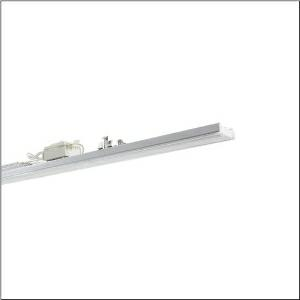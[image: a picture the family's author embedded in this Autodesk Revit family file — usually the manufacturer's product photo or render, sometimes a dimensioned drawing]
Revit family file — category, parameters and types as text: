
# Revit family: licross_21_recessed_mo_52te14dv4exg
name_source: partatom
category: Lighting Fixtures
units: mm (PartAtom-declared; Revit-internal decimal feet)

## family parameters
Cut with Voids When Loaded = No
Host = Face
Light Source = No
Part Type = Normal
Room Calculation Point = No
Round Connector Dimension = Use Diameter
Shared = No

## types (1)
- --- (1 x LED, 14200 lm, 85.3 W, 4000K)
    Apparent Load = 85 VA
    CIE Flux Codes = 56 84 97 100 100
    Color Rendering = 80
    Color Temperature = 4000K
    Default Elevation = 1800 mm
    Description = Licross 21 Recessed MO, luminaire insert, of sheet steel, galvanised, coil coated, white, length: 2.250mm, width: 66mm, height: 67mm, LED rated luminous flux: 14.200lm, light colour: 840, SDCM (Standard Deviation of Colour Matching)MacAdam ≤ 3 SDCM (initial), control gear: DALI 2, with plug, 5-pole, with phase selection, mains connection: 220..240V, AC, 50/60Hz, rated input power: 85W, internal wiring halogen-free, primary light control with lens, of plastic, primary optical cover: cover, of PMMA, light emission: direct distribution, primary light characteristic: asymmetric, protection rating (complete): IP54, insulation class (complete): insulation class I (protective earthing), certification: CE, ENEC, VDE, UKCA, protection symbol: D if used in an environment with non-conductive dust loads with corresponding accessories, impact resistance: IK06, permissible ambient temperature for indoor applications: -25..+35°C, corresponds to IFS (International Featured Standards) requirements for safety and quality in the food industry, reducing of maximum allowable ambient temperature of 5°C with ceiling mounting, LABS conformity tested according to VDMA 24364:2018-05, The light source and the operating device comply with the requirements of the Ecodesign Regulation (EU) 2019/2020 and are replaceable in accordance with this regulation, packaging unit: 1 piece
    Height = 58 mm
    Lamp = 1 x LED
    Lamp Light Flux = 14200 lm
    Lamp Power = 85.3 W
    Lamp count = 1
    Length = 2250 mm
    Luminous efficacy = 166 lm/W
    Manufacturer = Siteco
    ModVariant = No
    Model = 52TE14DV4EXG
    Mounting Place = Ceiling
    Mounting Type = Pendant
    Number of Poles = 1
    OnlyDefault = Yes
    Power Factor = 1
    Product Name = Licross 21 Recessed MO
    Product group = luminaire insert | ceiling pendant
    ProductGroupID = 901
    Protection Class = Protection class I
    Protection Degree = IP 54
    RLX_Detail_Level = 1
    RLX_Emergency_Light_Flux = 0 lm
    RLX_Emergency_Type = 0
    RLX_Emergency_Type_DB = No
    RlxData = <blob elided: 30201 chars, md5=32578309>
    Socket = socket
    Standby Power = 0 W
    System Light Flux = 14200 lm
    System Power = 85 W
    Type Comments = factory setting: luminous flux: 100 % | dim-lin: 254 | 390 mA
    Type Image = l_1296930.jpg
    URL = http://relux.com
    VarID = @adj_127967
    Voltage = 0 V
    Weight = 0.00 kg
    Width = 66 mm

## geometry (parser evidence)
native form markers: Blend x4, Sweep x13
no freeform markers — native parametric forms only
